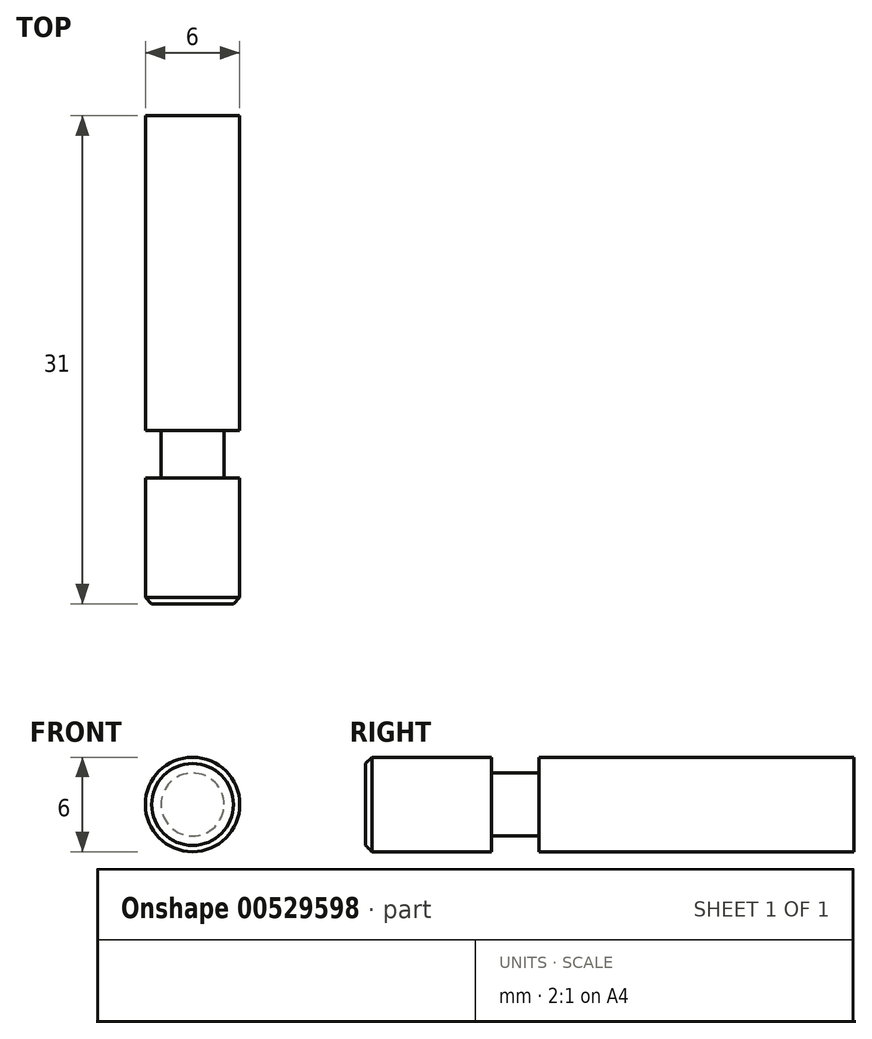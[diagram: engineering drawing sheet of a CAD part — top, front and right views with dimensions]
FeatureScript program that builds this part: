
annotation { "Feature Type Name" : "Feature", "Feature Type Description" : "" }
export const myFeature = defineFeature(function(context is Context, id is Id, definition is map)
    precondition{}
    {
        {
            var Q0;
            Q0=qCreatedBy(makeId("Front.planeOp"),FACE);
            var sketch = newSketch(context, id + "F0", { "sketchPlane" : qUnion([Q0])});
            skCircle(sketch, "E0", {"center": v(0, 0) * mm, "radius": 3 * mm});
            skSolve(sketch);
        }
        {
            var Q0;
            Q0 = qSketchRegion(id + "F0", true);
            extrude(context, id + "F1", {"entities" : qUnion([Q0]), "endBound" : BoundingType.SYMMETRIC, "depth" : 20 * mm, "offsetDistance" : 25 * mm});
        }
        {
            var Q0;
            Q0=makeQuery(id+"F1.opExtrude","CAP_FACE",FACE,{"disambiguationData":[OSD([sQuery(id+"F0.wireOp",EDGE,"E0")])],"isStart":false});
            var sketch = newSketch(context, id + "F2", { "sketchPlane" : qUnion([Q0])});
            skCircle(sketch, "E1", {"center": v(0, 0) * mm, "radius": 2 * mm});
            skSolve(sketch);
        }
        {
            var Q0;
            Q0 = qSketchRegion(id + "F2", true);
            extrude(context, id + "F3", {"entities" : qUnion([Q0]), "operationType" : NewBodyOperationType.ADD, "depth" : 3 * mm, "offsetDistance" : 25 * mm});
        }
        {
            var Q0;
            Q0=makeQuery(id+"F3.opExtrude","CAP_FACE",FACE,{"disambiguationData":[OSD([sQuery(id+"F2.wireOp",EDGE,"E1")])],"isStart":false});
            var sketch = newSketch(context, id + "F4", { "sketchPlane" : qUnion([Q0])});
            skCircle(sketch, "E2", {"center": v(0, 0) * mm, "radius": 3 * mm});
            skSolve(sketch);
        }
        {
            var Q0;
            Q0 = qSketchRegion(id + "F4", true);
            extrude(context, id + "F5", {"entities" : qUnion([Q0]), "operationType" : NewBodyOperationType.ADD, "depth" : (31 - 23) * mm, "offsetDistance" : 25 * mm});
        }
        {
            var Q0;
            Q0=makeQuery(id+"F5.opExtrude","CAP_EDGE",EDGE,{"disambiguationData":[OSD([sQuery(id+"F4.wireOp",EDGE,"E2")])],"isStart":false});
            chamfer(context, id + "F6", {"entities" : qUnion([Q0]), "width" : 0.4 * mm, "tangentPropagation" : true});
        }
    });
